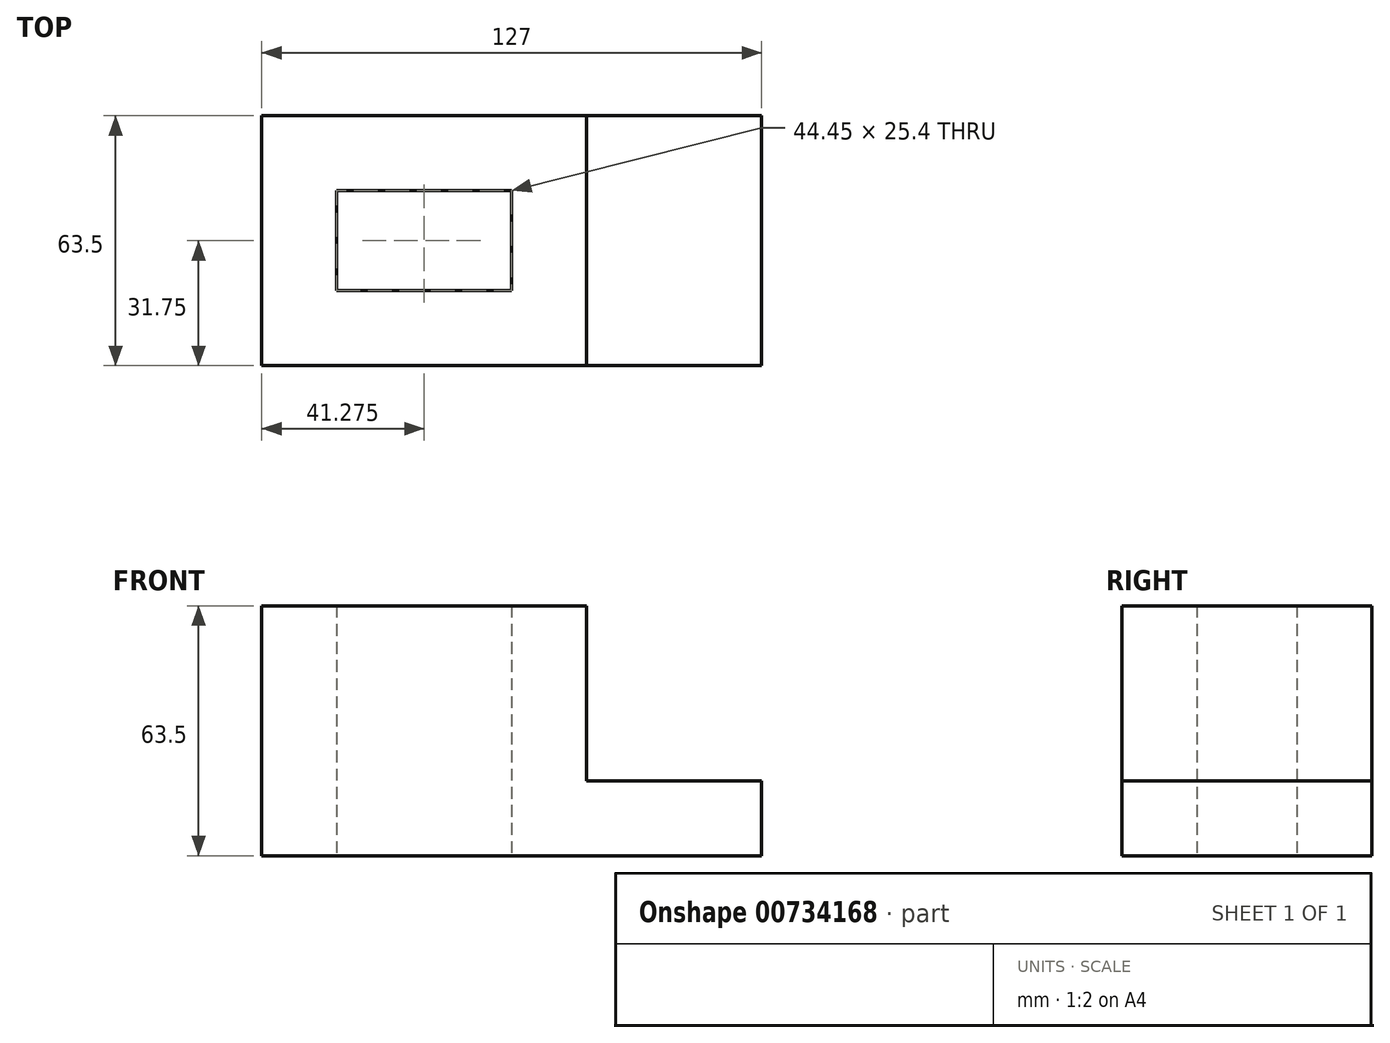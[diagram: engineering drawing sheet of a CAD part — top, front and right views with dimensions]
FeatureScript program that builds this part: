
annotation { "Feature Type Name" : "Feature", "Feature Type Description" : "" }
export const myFeature = defineFeature(function(context is Context, id is Id, definition is map)
    precondition{}
    {
        {
            var Q0;
            Q0=qCreatedBy(makeId("Top.planeOp"),FACE);
            var sketch = newSketch(context, id + "F0", { "sketchPlane" : qUnion([Q0])});
            skLineSegment(sketch, "E0.bottom", {"start": v(0, 63.5) * mm, "end": v(-82.55, 63.5) * mm});
            skLineSegment(sketch, "E0.top", {"start": v(0, 0) * mm, "end": v(-82.55, 0) * mm});
            skLineSegment(sketch, "E0.left", {"start": v(0, 63.5) * mm, "end": v(0, 0) * mm});
            skLineSegment(sketch, "E0.right", {"start": v(-82.55, 63.5) * mm, "end": v(-82.55, 0) * mm});
            skLineSegment(sketch, "E1.left", {"start": v(0, 63.5) * mm, "end": v(0, 63.5) * mm});
            skLineSegment(sketch, "E1.right", {"start": v(-82.55, 63.5) * mm, "end": v(-82.55, 63.5) * mm});
            skLineSegment(sketch, "E2.bottom", {"start": v(-63.5, 44.45) * mm, "end": v(-19.05, 44.45) * mm});
            skLineSegment(sketch, "E2.top", {"start": v(-63.5, 19.05) * mm, "end": v(-19.05, 19.05) * mm});
            skLineSegment(sketch, "E2.left", {"start": v(-63.5, 44.45) * mm, "end": v(-63.5, 19.05) * mm});
            skLineSegment(sketch, "E2.right", {"start": v(-19.05, 44.45) * mm, "end": v(-19.05, 19.05) * mm});
            skLineSegment(sketch, "E3", {"start": v(0, 63.5) * mm, "end": v(44.45, 63.5) * mm});
            skLineSegment(sketch, "E4", {"start": v(44.45, 63.5) * mm, "end": v(44.45, 0) * mm});
            skLineSegment(sketch, "E5", {"start": v(0, 0) * mm, "end": v(44.45, 0) * mm});
            skSolve(sketch);
        }
        {
            var Q0;
            Q0=makeQuery(id+"F0.imprint","IMPRINT",FACE,{"disambiguationData":[TD([[makeQuery(id+"F0.imprint","IMPRINT",EDGE,{"derivedFrom":sQuery(id+"F0.wireOp",EDGE,"E0.top")}),-1.0]])]});
            extrude(context, id + "F1", {"entities" : qUnion([Q0]), "depth" : 63.5 * mm, "offsetDistance" : 25.4 * mm});
        }
        {
            var Q0;
            Q0=makeQuery(id+"F0.imprint","IMPRINT",FACE,{"disambiguationData":[TD([[makeQuery(id+"F0.imprint","IMPRINT",EDGE,{"derivedFrom":sQuery(id+"F0.wireOp",EDGE,"E0.left")}),1.0]])]});
            extrude(context, id + "F2", {"entities" : qUnion([Q0]), "operationType" : NewBodyOperationType.ADD, "depth" : 19.05 * mm, "offsetDistance" : 25.4 * mm});
        }
    });
